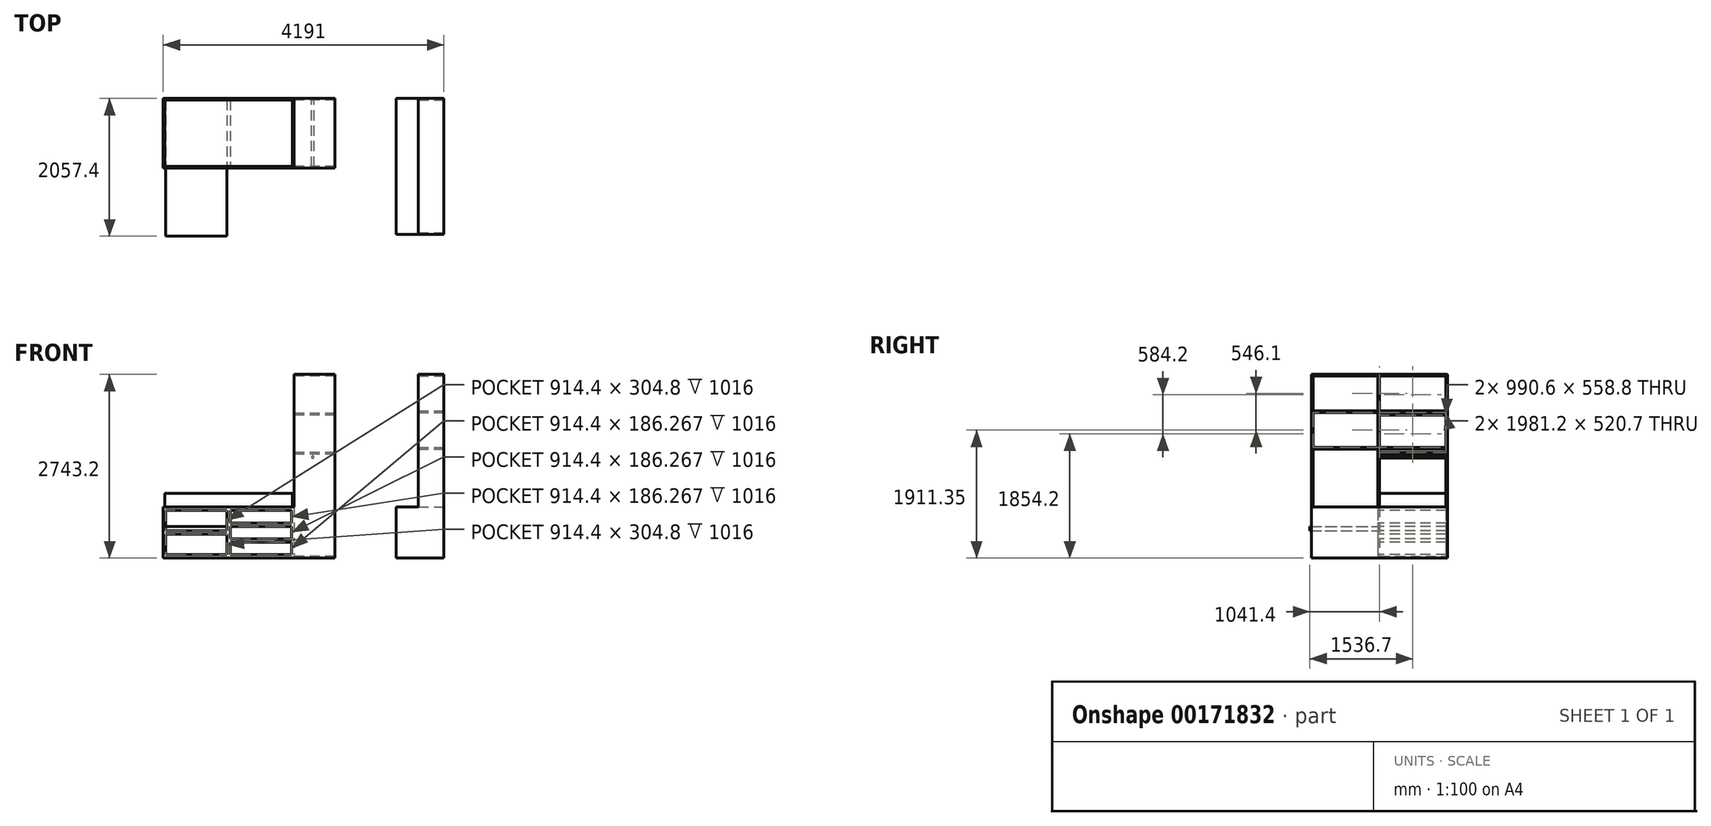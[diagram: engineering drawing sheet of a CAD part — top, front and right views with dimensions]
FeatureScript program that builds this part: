
annotation { "Feature Type Name" : "Feature", "Feature Type Description" : "" }
export const myFeature = defineFeature(function(context is Context, id is Id, definition is map)
    precondition{}
    {
        {
            var Q0;
            Q0=qCreatedBy(makeId("Top.planeOp"),FACE);
            var sketch = newSketch(context, id + "F0", { "sketchPlane" : qUnion([Q0])});
            skLineSegment(sketch, "E0.bottom", {"start": v(0, 0) * mm, "end": v(1955.8, 0) * mm});
            skLineSegment(sketch, "E0.top", {"start": v(0, -1041.4) * mm, "end": v(1955.8, -1041.4) * mm});
            skLineSegment(sketch, "E0.left", {"start": v(0, 0) * mm, "end": v(0, -1041.4) * mm});
            skLineSegment(sketch, "E0.right", {"start": v(1955.8, 0) * mm, "end": v(1955.8, -1041.4) * mm});
            skSolve(sketch);
        }
        {
            var Q0;
            Q0 = qSketchRegion(id + "F0", true);
            extrude(context, id + "F1", {"entities" : qUnion([Q0]), "depth" : 762 * mm});
        }
        {
            var Q0;
            Q0=makeQuery(id+"F1.opExtrude","CAP_FACE",FACE,{"disambiguationData":[OSD([sQuery(id+"F0.wireOp",EDGE,"E0.bottom"),sQuery(id+"F0.wireOp",EDGE,"E0.top"),sQuery(id+"F0.wireOp",EDGE,"E0.left"),sQuery(id+"F0.wireOp",EDGE,"E0.right")])],"isStart":false});
            var sketch = newSketch(context, id + "F2", { "sketchPlane" : qUnion([Q0])});
            skLineSegment(sketch, "E1.bottom", {"start": v(50.8, -25.4) * mm, "end": v(1905, -25.4) * mm});
            skLineSegment(sketch, "E1.top", {"start": v(50.8, -1016) * mm, "end": v(1905, -1016) * mm});
            skLineSegment(sketch, "E1.left", {"start": v(25.4, -50.8) * mm, "end": v(25.4, -990.6) * mm});
            skLineSegment(sketch, "E1.right", {"start": v(1930.4, -50.8) * mm, "end": v(1930.4, -990.6) * mm});
            skPoint(sketch, "E2.visualSharp", {"position": v(25.4, -25.4) * mm});
            skArc(sketch, "E2.filletArc", {"start": v(50.8, -25.4) * mm, "mid": v(32.84, -32.84) * mm, "end": v(25.4, -50.8) * mm});
            skPoint(sketch, "E3.visualSharp", {"position": v(25.4, -1016) * mm});
            skArc(sketch, "E3.filletArc", {"start": v(25.4, -990.6) * mm, "mid": v(32.84, -1008.56) * mm, "end": v(50.8, -1016) * mm});
            skPoint(sketch, "E4.visualSharp", {"position": v(1930.4, -1016) * mm});
            skArc(sketch, "E4.filletArc", {"start": v(1905, -1016) * mm, "mid": v(1922.96, -1008.56) * mm, "end": v(1930.4, -990.6) * mm});
            skPoint(sketch, "E5.visualSharp", {"position": v(1930.4, -25.4) * mm});
            skArc(sketch, "E5.filletArc", {"start": v(1930.4, -50.8) * mm, "mid": v(1922.96, -32.84) * mm, "end": v(1905, -25.4) * mm});
            skSolve(sketch);
        }
        {
            var Q0;
            Q0 = qSketchRegion(id + "F2", true);
            extrude(context, id + "F3", {"entities" : qUnion([Q0]), "operationType" : NewBodyOperationType.ADD, "depth" : 203.2 * mm});
        }
        {
            var Q0;
            Q0=makeQuery(id+"F1.opExtrude","SWEPT_FACE",FACE,{"disambiguationData":[OSD([sQuery(id+"F0.wireOp",EDGE,"E0.top")])]});
            var sketch = newSketch(context, id + "F4", { "sketchPlane" : qUnion([Q0])});
            skLineSegment(sketch, "E6.bottom", {"start": v(38.1, 711.2) * mm, "end": v(952.5, 711.2) * mm});
            skLineSegment(sketch, "E6.top", {"start": v(38.1, 406.4) * mm, "end": v(952.5, 406.4) * mm});
            skLineSegment(sketch, "E6.left", {"start": v(38.1, 711.2) * mm, "end": v(38.1, 406.4) * mm});
            skLineSegment(sketch, "E6.right", {"start": v(952.5, 711.2) * mm, "end": v(952.5, 406.4) * mm});
            skLineSegment(sketch, "E7.bottom", {"start": v(38.1, 355.6) * mm, "end": v(952.5, 355.6) * mm});
            skLineSegment(sketch, "E7.top", {"start": v(38.1, 50.8) * mm, "end": v(952.5, 50.8) * mm});
            skLineSegment(sketch, "E7.left", {"start": v(38.1, 355.6) * mm, "end": v(38.1, 50.8) * mm});
            skLineSegment(sketch, "E7.right", {"start": v(952.5, 355.6) * mm, "end": v(952.5, 50.8) * mm});
            skLineSegment(sketch, "E8.bottom", {"start": v(1003.3, 711.2) * mm, "end": v(1917.7, 711.2) * mm});
            skLineSegment(sketch, "E8.top", {"start": v(1003.3, 524.93) * mm, "end": v(1917.7, 524.93) * mm});
            skLineSegment(sketch, "E8.left", {"start": v(1003.3, 711.2) * mm, "end": v(1003.3, 524.93) * mm});
            skLineSegment(sketch, "E8.right", {"start": v(1917.7, 711.2) * mm, "end": v(1917.7, 524.93) * mm});
            skLineSegment(sketch, "E9.bottom", {"start": v(1003.3, 474.13) * mm, "end": v(1917.7, 474.13) * mm});
            skLineSegment(sketch, "E9.top", {"start": v(1003.3, 287.87) * mm, "end": v(1917.7, 287.87) * mm});
            skLineSegment(sketch, "E9.left", {"start": v(1003.3, 474.13) * mm, "end": v(1003.3, 287.87) * mm});
            skLineSegment(sketch, "E9.right", {"start": v(1917.7, 474.13) * mm, "end": v(1917.7, 287.87) * mm});
            skLineSegment(sketch, "E10.bottom", {"start": v(1003.3, 237.07) * mm, "end": v(1917.7, 237.07) * mm});
            skLineSegment(sketch, "E10.top", {"start": v(1003.3, 50.8) * mm, "end": v(1917.7, 50.8) * mm});
            skLineSegment(sketch, "E10.left", {"start": v(1003.3, 237.07) * mm, "end": v(1003.3, 50.8) * mm});
            skLineSegment(sketch, "E10.right", {"start": v(1917.7, 237.07) * mm, "end": v(1917.7, 50.8) * mm});
            skSolve(sketch);
        }
        {
            var Q0;
            Q0 = qSketchRegion(id + "F4", true);
            extrude(context, id + "F5", {"entities" : qUnion([Q0]), "operationType" : NewBodyOperationType.REMOVE, "oppositeDirection" : true, "depth" : 1016 * mm});
        }
        {
            var Q0;
            Q0=makeQuery(id+"F1.opExtrude","SWEPT_FACE",FACE,{"disambiguationData":[OSD([sQuery(id+"F0.wireOp",EDGE,"E0.top")])]});
            var sketch = newSketch(context, id + "F6", { "sketchPlane" : qUnion([Q0])});
            skLineSegment(sketch, "E11.bottom", {"start": v(38.1, 406.4) * mm, "end": v(952.5, 406.4) * mm});
            skLineSegment(sketch, "E11.top", {"start": v(38.1, 472.27) * mm, "end": v(952.5, 472.27) * mm});
            skLineSegment(sketch, "E11.left", {"start": v(38.1, 406.4) * mm, "end": v(38.1, 472.27) * mm});
            skLineSegment(sketch, "E11.right", {"start": v(952.5, 406.4) * mm, "end": v(952.5, 472.27) * mm});
            skSolve(sketch);
        }
        {
            var Q0;
            Q0 = qSketchRegion(id + "F6", true);
            extrude(context, id + "F7", {"entities" : qUnion([Q0]), "depth" : 1016 * mm});
        }
        {
            var Q0;
            Q0=makeQuery(id+"F1.opExtrude","SWEPT_FACE",FACE,{"disambiguationData":[OSD([sQuery(id+"F0.wireOp",EDGE,"E0.right")])]});
            var sketch = newSketch(context, id + "F8", { "sketchPlane" : qUnion([Q0])});
            skLineSegment(sketch, "E12.bottom", {"start": v(-1041.4, 0) * mm, "end": v(0, 0) * mm});
            skLineSegment(sketch, "E12.top", {"start": v(-1041.4, 2743.2) * mm, "end": v(0, 2743.2) * mm});
            skLineSegment(sketch, "E12.left", {"start": v(-1041.4, 0) * mm, "end": v(-1041.4, 2743.2) * mm});
            skLineSegment(sketch, "E12.right", {"start": v(0, 0) * mm, "end": v(0, 2743.2) * mm});
            skLineSegment(sketch, "E13.bottom", {"start": v(-1016, 2133.6) * mm, "end": v(-25.4, 2133.6) * mm});
            skLineSegment(sketch, "E13.top", {"start": v(-1016, 1574.8) * mm, "end": v(-25.4, 1574.8) * mm});
            skLineSegment(sketch, "E13.left", {"start": v(-1016, 2133.6) * mm, "end": v(-1016, 1574.8) * mm});
            skLineSegment(sketch, "E13.right", {"start": v(-25.4, 2133.6) * mm, "end": v(-25.4, 1574.8) * mm});
            skLineSegment(sketch, "E14.bottom", {"start": v(-1016, 1549.4) * mm, "end": v(-25.4, 1549.4) * mm});
            skLineSegment(sketch, "E14.top", {"start": v(-1016, 25.4) * mm, "end": v(-25.4, 25.4) * mm});
            skLineSegment(sketch, "E14.left", {"start": v(-1016, 1549.4) * mm, "end": v(-1016, 25.4) * mm});
            skLineSegment(sketch, "E14.right", {"start": v(-25.4, 1549.4) * mm, "end": v(-25.4, 25.4) * mm});
            skLineSegment(sketch, "E15.bottom", {"start": v(-1016, 2717.8) * mm, "end": v(-25.4, 2717.8) * mm});
            skLineSegment(sketch, "E15.top", {"start": v(-1016, 2159) * mm, "end": v(-25.4, 2159) * mm});
            skLineSegment(sketch, "E15.left", {"start": v(-1016, 2717.8) * mm, "end": v(-1016, 2159) * mm});
            skLineSegment(sketch, "E15.right", {"start": v(-25.4, 2717.8) * mm, "end": v(-25.4, 2159) * mm});
            skSolve(sketch);
        }
        {
            var Q0;
            Q0 = qSketchRegion(id + "F8", true);
            extrude(context, id + "F9", {"entities" : qUnion([Q0]), "operationType" : NewBodyOperationType.ADD, "depth" : 609.6 * mm});
        }
        {
            var Q0;
            Q0=makeQuery(id+"F9.opExtrude","SWEPT_FACE",FACE,{"disambiguationData":[OSD([sQuery(id+"F8.wireOp",EDGE,"E14.right")])]});
            var sketch = newSketch(context, id + "F10", { "sketchPlane" : qUnion([Q0])});
            skCircle(sketch, "E16", {"center": v(2232.32, 1508.6) * mm, "radius": 16.8 * mm});
            skSolve(sketch);
        }
        {
            var Q0;
            Q0 = qSketchRegion(id + "F10", true);
            var Q1;
            Q1=makeQuery(id+"F9.opExtrude","SWEPT_FACE",FACE,{"disambiguationData":[OSD([sQuery(id+"F8.wireOp",EDGE,"E14.left")])]});
            extrude(context, id + "F11", {"entities" : qUnion([Q0]), "operationType" : NewBodyOperationType.ADD, "endBound" : BoundingType.UP_TO_SURFACE, "endBoundEntityFace" : qUnion([Q1]), "depth" : 25.4 * mm});
        }
        {
            var Q0;
            Q0=qCreatedBy(makeId("Top.planeOp"),FACE);
            var sketch = newSketch(context, id + "F12", { "sketchPlane" : qUnion([Q0])});
            skLineSegment(sketch, "E17.bottom", {"start": v(4191, 0) * mm, "end": v(3479.8, 0) * mm});
            skLineSegment(sketch, "E17.top", {"start": v(4191, -2032) * mm, "end": v(3479.8, -2032) * mm});
            skLineSegment(sketch, "E17.left", {"start": v(4191, 0) * mm, "end": v(4191, -2032) * mm});
            skLineSegment(sketch, "E17.right", {"start": v(3479.8, 0) * mm, "end": v(3479.8, -2032) * mm});
            skLineSegment(sketch, "E18.bottom", {"start": v(0, 0) * mm, "end": v(4191, 0) * mm, "construction": true});
            skLineSegment(sketch, "E18.top", {"start": v(0, -2057.4) * mm, "end": v(4191, -2057.4) * mm, "construction": true});
            skLineSegment(sketch, "E18.left", {"start": v(0, 0) * mm, "end": v(0, -2057.4) * mm, "construction": true});
            skLineSegment(sketch, "E18.right", {"start": v(4191, 0) * mm, "end": v(4191, -2057.4) * mm, "construction": true});
            skSolve(sketch);
        }
        {
            var Q0;
            Q0 = qSketchRegion(id + "F12", true);
            extrude(context, id + "F13", {"entities" : qUnion([Q0]), "depth" : 762 * mm});
        }
        {
            var Q0;
            Q0=makeQuery(id+"F13.opExtrude","SWEPT_FACE",FACE,{"disambiguationData":[OSD([sQuery(id+"F12.wireOp",EDGE,"E17.left")])]});
            var sketch = newSketch(context, id + "F14", { "sketchPlane" : qUnion([Q0])});
            skLineSegment(sketch, "E19", {"start": v(-2032, 762) * mm, "end": v(-2032, 2743.2) * mm});
            skLineSegment(sketch, "E20", {"start": v(-2032, 2743.2) * mm, "end": v(0, 2743.2) * mm});
            skLineSegment(sketch, "E21", {"start": v(0, 2743.2) * mm, "end": v(0, 762) * mm});
            skLineSegment(sketch, "E22.bottom", {"start": v(-2006.6, 2717.8) * mm, "end": v(-25.4, 2717.8) * mm});
            skLineSegment(sketch, "E22.top", {"start": v(-2006.6, 2197.1) * mm, "end": v(-25.4, 2197.1) * mm});
            skLineSegment(sketch, "E22.left", {"start": v(-2006.6, 2717.8) * mm, "end": v(-2006.6, 2197.1) * mm});
            skLineSegment(sketch, "E22.right", {"start": v(-25.4, 2717.8) * mm, "end": v(-25.4, 2197.1) * mm});
            skLineSegment(sketch, "E23.bottom", {"start": v(-2006.6, 2171.7) * mm, "end": v(-25.4, 2171.7) * mm});
            skLineSegment(sketch, "E23.top", {"start": v(-2006.6, 1651) * mm, "end": v(-25.4, 1651) * mm});
            skLineSegment(sketch, "E23.left", {"start": v(-2006.6, 2171.7) * mm, "end": v(-2006.6, 1651) * mm});
            skLineSegment(sketch, "E23.right", {"start": v(-25.4, 2171.7) * mm, "end": v(-25.4, 1651) * mm});
            skLineSegment(sketch, "E24", {"start": v(-2032, 762) * mm, "end": v(-2006.6, 762) * mm});
            skLineSegment(sketch, "E25", {"start": v(-2006.6, 762) * mm, "end": v(-2006.6, 1625.6) * mm});
            skLineSegment(sketch, "E26", {"start": v(0, 762) * mm, "end": v(-25.4, 762) * mm});
            skLineSegment(sketch, "E27", {"start": v(-25.4, 762) * mm, "end": v(-25.4, 1625.6) * mm});
            skLineSegment(sketch, "E28", {"start": v(-2006.6, 1625.6) * mm, "end": v(-25.4, 1625.6) * mm});
            skSolve(sketch);
        }
        {
            var Q0;
            Q0 = qSketchRegion(id + "F14", true);
            extrude(context, id + "F15", {"entities" : qUnion([Q0]), "operationType" : NewBodyOperationType.ADD, "oppositeDirection" : true, "depth" : 381 * mm});
        }
    });
